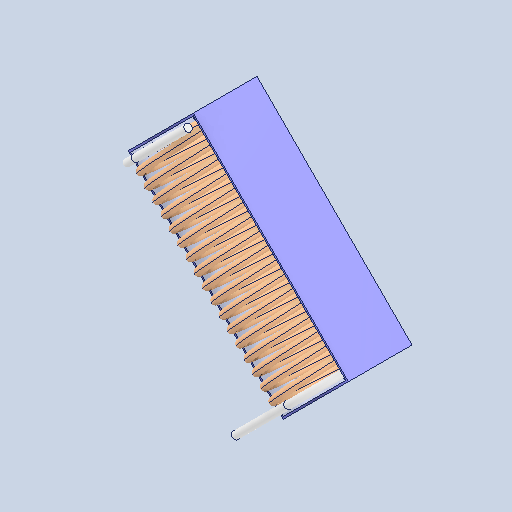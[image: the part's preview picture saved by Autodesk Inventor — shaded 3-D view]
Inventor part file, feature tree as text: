
AUTODESK INVENTOR PART (.ipt)
format: ipt  version: 2025 (Build 290162000, 162)  size: 715,264 bytes
history: native  units: mm
features: sweep x1, other x1
ambient origin geometry x8: Origin, YZ Plane, XZ Plane, XY Plane, X Axis, Y Axis, Z Axis, Center Point
bodies: Solid1 (feature_tree), Solid2 (feature_tree)
feature tree (2):
  sweep  "Sweep9"
  other  "Cut-Extrude1"
